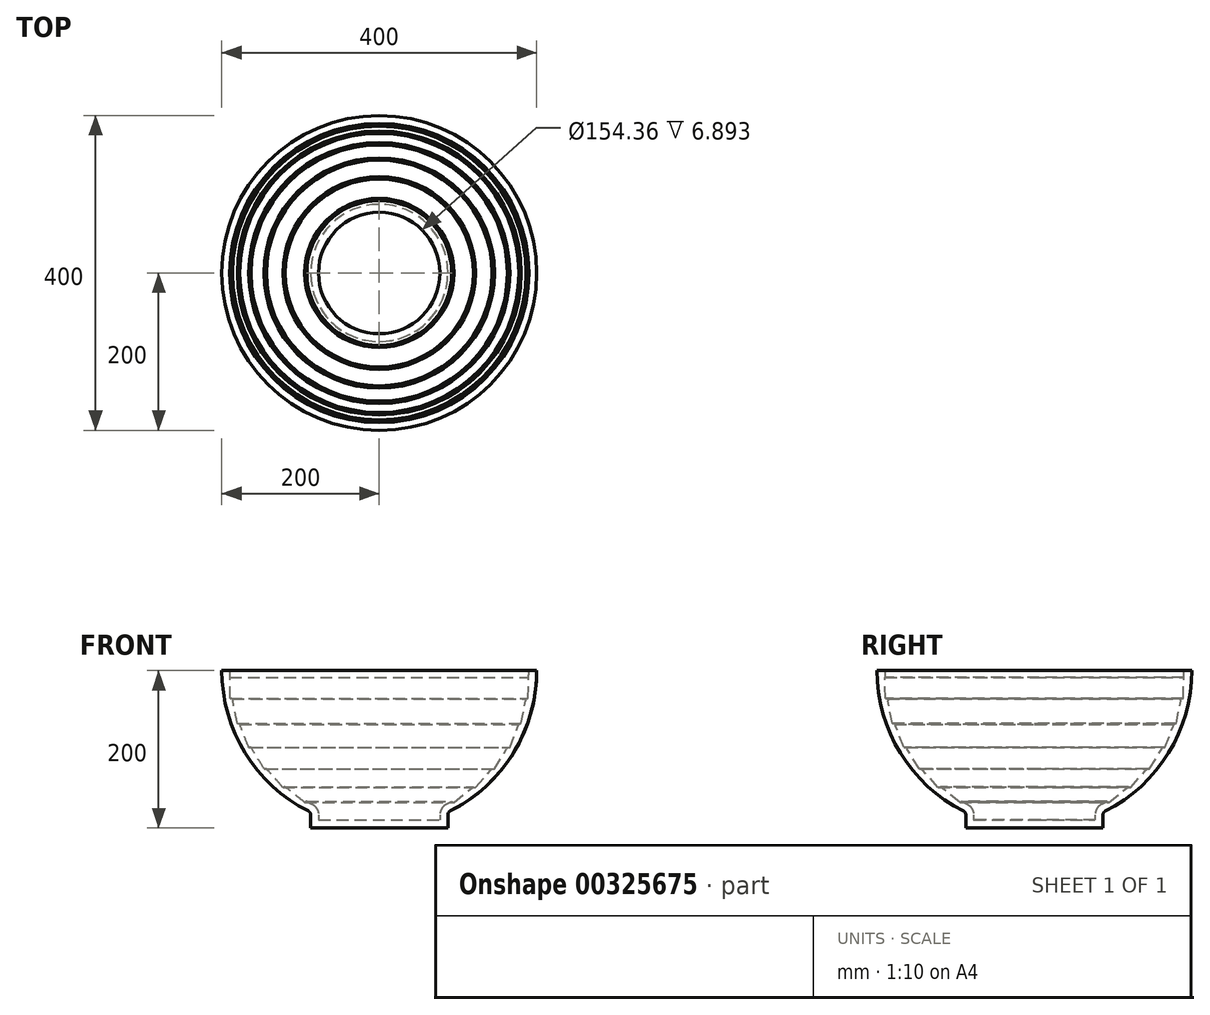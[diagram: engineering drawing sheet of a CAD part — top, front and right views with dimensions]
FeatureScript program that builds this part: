
annotation { "Feature Type Name" : "Feature", "Feature Type Description" : "" }
export const myFeature = defineFeature(function(context is Context, id is Id, definition is map)
    precondition{}
    {
        {
            var Q0;
            Q0=qCreatedBy(makeId("Front.planeOp"),FACE);
            var sketch = newSketch(context, id + "F0", { "sketchPlane" : qUnion([Q0])});
            skLineSegment(sketch, "E0", {"start": v(0, -200) * mm, "end": v(0, 0) * mm});
            skLineSegment(sketch, "E1", {"start": v(0, 0) * mm, "end": v(200, 0) * mm});
            skLineSegment(sketch, "E2", {"start": v(200, 0) * mm, "end": v(200, 0) * mm});
            skArc(sketch, "E3", {"start": v(0, -200) * mm, "mid": v(141.42, -141.42) * mm, "end": v(200, 0) * mm});
            skArc(sketch, "E4", {"start": v(200, 0) * mm, "mid": v(-141.42, 141.42) * mm, "end": v(0, -200) * mm, "construction": true});
            skLineSegment(sketch, "E5", {"start": v(0, -200) * mm, "end": v(87.18, -200) * mm});
            skLineSegment(sketch, "E6", {"start": v(87.18, -200) * mm, "end": v(87.18, -180) * mm});
            skPoint(sketch, "E7.orphan", {"position": v(-200, 0) * mm});
            skSolve(sketch);
        }
        {
            var Q0;
            {var subQ0=sQuery(id+"F0.wireOp",EDGE,"E0");Q0=makeQuery(id+"F0.imprint","IMPRINT",FACE,{"disambiguationData":[TD([[makeQuery(id+"F0.imprint","IMPRINT",EDGE,{"derivedFrom":subQ0}),-1.0]])]});}
            var Q1;
            {var subQ0=sQuery(id+"F0.wireOp",EDGE,"E5");Q1=makeQuery(id+"F0.imprint","IMPRINT",FACE,{"disambiguationData":[TD([[makeQuery(id+"F0.imprint","IMPRINT",EDGE,{"derivedFrom":subQ0}),1.0]])]});}
            var Q2;
            Q2=sQuery(id+"F0.wireOp",EDGE,"E0");
            revolve(context, id + "F1", {"entities" : qUnion([Q0, Q1]), "axis" : qUnion([Q2]), "revolveType" : RevolveType.FULL});
        }
        {
            var Q0;
            Q0=makeQuery(id+"F1.opRevolve","SWEPT_EDGE",EDGE,{"disambiguationData":[OSD([sQuery(id+"F0.wireOp",EDGE,"E3"),sQuery(id+"F0.wireOp",EDGE,"E6")])]});
            fillet(context, id + "F2", {"entities" : qUnion([Q0]), "radius" : 5 * mm, "tangentPropagation" : true, "allowEdgeOverflow" : false});
        }
        {
            var Q0;
            Q0=makeQuery(id+"F1.opRevolve","SWEPT_FACE",FACE,{"disambiguationData":[OSD([sQuery(id+"F0.wireOp",EDGE,"E1")])]});
            shell(context, id + "F3", {"entities" : qUnion([Q0]), "thickness" : 10 * mm});
        }
        {
            var Q0;
            {var subQ0=sQuery(id+"F0.wireOp",EDGE,"E0");Q0=makeQuery(id+"F0.imprint","IMPRINT",FACE,{"disambiguationData":[TD([[makeQuery(id+"F0.imprint","IMPRINT",EDGE,{"derivedFrom":subQ0}),-1.0]])]});}
            var sketch = newSketch(context, id + "F4", { "sketchPlane" : qUnion([Q0])});
            skLineSegment(sketch, "E8.30.0", {"start": v(94.71, -167.53) * mm, "end": v(92, -166.24) * mm});
            skLineSegment(sketch, "E8.31.0", {"start": v(122.36, -148.54) * mm, "end": v(119.47, -147.74) * mm});
            skLineSegment(sketch, "E8.32.0", {"start": v(146.3, -125.03) * mm, "end": v(143.31, -124.75) * mm});
            skLineSegment(sketch, "E8.33.0", {"start": v(165.79, -97.73) * mm, "end": v(162.8, -97.96) * mm});
            skLineSegment(sketch, "E8.34.0", {"start": v(180.24, -67.46) * mm, "end": v(177.34, -68.2) * mm});
            skLineSegment(sketch, "E8.35.0", {"start": v(189.22, -35.13) * mm, "end": v(186.49, -36.38) * mm});
            skArc(sketch, "E9", {"start": v(-0.05, -190) * mm, "mid": v(134.33, -134.37) * mm, "end": v(190, 0) * mm});
            skArc(sketch, "E10", {"start": v(190, 0) * mm, "mid": v(-134.33, 134.37) * mm, "end": v(-0.05, -190) * mm, "construction": true});
            skLineSegment(sketch, "E11", {"start": v(190, 0) * mm, "end": v(189.22, -35.13) * mm});
            skLineSegment(sketch, "E12", {"start": v(186.49, -36.38) * mm, "end": v(180.24, -67.46) * mm});
            skLineSegment(sketch, "E13", {"start": v(165.79, -97.73) * mm, "end": v(177.34, -68.2) * mm});
            skLineSegment(sketch, "E14", {"start": v(146.3, -125.03) * mm, "end": v(162.8, -97.96) * mm});
            skLineSegment(sketch, "E15", {"start": v(122.36, -148.54) * mm, "end": v(143.31, -124.75) * mm});
            skLineSegment(sketch, "E16", {"start": v(94.71, -167.53) * mm, "end": v(119.47, -147.74) * mm});
            skSolve(sketch);
        }
        {
            var Q0;
            Q0 = qSketchRegion(id + "F4", true);
            var Q1;
            Q1=sQuery(id+"F0.wireOp",EDGE,"E0");
            revolve(context, id + "F5", {"entities" : qUnion([Q0]), "axis" : qUnion([Q1]), "revolveType" : RevolveType.FULL});
        }
        {
            var Q0;
            Q0=makeQuery(id+"F5.opRevolve","SWEPT_BODY",BODY,{"disambiguationData":[OSD([sQuery(id+"F4.wireOp",EDGE,"24A7FfYV-PEMF-Z90R-V4Uk-vumOBUulam6M"),sQuery(id+"F4.wireOp",EDGE,"3QzNC3UW-SJrg-zFh9-Ekz0-N955zFM6e3wE"),sQuery(id+"F4.wireOp",EDGE,"E9")])]});
            var Q1;
            Q1=makeQuery(id+"F5.opRevolve","SWEPT_BODY",BODY,{"disambiguationData":[OSD([sQuery(id+"F4.wireOp",EDGE,"E8.35.0"),sQuery(id+"F4.wireOp",EDGE,"E9"),sQuery(id+"F4.wireOp",EDGE,"E11")])]});
            var Q2;
            Q2=makeQuery(id+"F5.opRevolve","SWEPT_BODY",BODY,{"disambiguationData":[OSD([sQuery(id+"F4.wireOp",EDGE,"E8.34.0"),sQuery(id+"F4.wireOp",EDGE,"E9"),sQuery(id+"F4.wireOp",EDGE,"E12")])]});
            var Q3;
            Q3=makeQuery(id+"F5.opRevolve","SWEPT_BODY",BODY,{"disambiguationData":[OSD([sQuery(id+"F4.wireOp",EDGE,"E8.33.0"),sQuery(id+"F4.wireOp",EDGE,"E9"),sQuery(id+"F4.wireOp",EDGE,"E13")])]});
            var Q4;
            Q4=makeQuery(id+"F5.opRevolve","SWEPT_BODY",BODY,{"disambiguationData":[OSD([sQuery(id+"F4.wireOp",EDGE,"E8.32.0"),sQuery(id+"F4.wireOp",EDGE,"E9"),sQuery(id+"F4.wireOp",EDGE,"E14")])]});
            var Q5;
            Q5=makeQuery(id+"F5.opRevolve","SWEPT_BODY",BODY,{"disambiguationData":[OSD([sQuery(id+"F4.wireOp",EDGE,"E8.31.0"),sQuery(id+"F4.wireOp",EDGE,"E9"),sQuery(id+"F4.wireOp",EDGE,"E15")])]});
            var Q6;
            Q6=makeQuery(id+"F5.opRevolve","SWEPT_BODY",BODY,{"disambiguationData":[OSD([sQuery(id+"F4.wireOp",EDGE,"E8.30.0"),sQuery(id+"F4.wireOp",EDGE,"E9"),sQuery(id+"F4.wireOp",EDGE,"E16")])]});
            var Q7;
            Q7=makeQuery(id+"F1.opRevolve","SWEPT_BODY",BODY,{"disambiguationData":[OSD([sQuery(id+"F0.wireOp",EDGE,"E0"),sQuery(id+"F0.wireOp",EDGE,"E1"),sQuery(id+"F0.wireOp",EDGE,"E3"),sQuery(id+"F0.wireOp",EDGE,"E5"),sQuery(id+"F0.wireOp",EDGE,"E6")])]});
            booleanBodies(context, id + "F6", {"operationType" : BooleanOperationType.SUBTRACTION, "tools" : qUnion([Q0, Q1, Q2, Q3, Q4, Q5, Q6]), "targets" : qUnion([Q7])});
        }
    });
